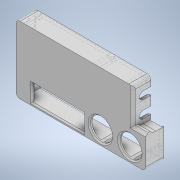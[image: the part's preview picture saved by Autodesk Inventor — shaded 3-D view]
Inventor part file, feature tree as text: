
AUTODESK INVENTOR PART (.ipt)
format: ipt  version: 2021 (Build 250183000, 183)  size: 477,696 bytes
history: native  units: mm
features: sketch x21, extrude x19, fillet x4, chamfer x4, hole x2
ambient origin geometry x8: Origin, YZ Plane, XZ Plane, XY Plane, X Axis, Y Axis, Z Axis, Center Point
bodies: Solid1 (feature_tree)
feature tree (50):
  extrude  "Extrusion1"  Depth=52.0mm
  extrude  "Extrusion2"  Depth=50.0mm
  extrude  "Extrusion3"  Depth=2.0mm
  extrude  "Extrusion4"  Depth=2.0mm
  fillet  "Fillet1"  Radius=2.0mm
  chamfer  "Chamfer1"  Distance=12.0mm
  extrude  "Extrusion5"  Depth=10.4mm
  extrude  "Extrusion6"  Depth=10.4mm
  extrude  "Extrusion7"  Depth=17.0mm
  extrude  "Extrusion8"  Depth=2.0mm
  extrude  "Extrusion9"  Depth=2.0mm
  chamfer  "Chamfer2"  Distance=2.0mm
  fillet  "Fillet2"  Radius=3.0mm
  extrude  "Extrusion10"  Depth=2.0mm
  fillet  "Fillet3"  Radius=29.0mm
  chamfer  "Chamfer3"  Distance=20.0mm
  extrude  "Extrusion11"  Depth=2.0mm TaperAngle=0.0deg
  extrude  "Extrusion12"  Depth=11.0mm
  hole  "Hole1"  [1 undecoded]
  extrude  "Extrusion13"  TaperAngle=0.0deg  [1 undecoded]
  hole  "Hole2"  [1 undecoded]
  extrude  "Extrusion14"  Depth=12.0mm
  extrude  "Extrusion15"  Depth=2.0mm TaperAngle=45.0deg
  extrude  "Extrusion16"  Depth=3.0mm
  extrude  "Extrusion17"  Depth=2.0mm
  extrude  "Extrusion20"  Depth=2.0mm
  fillet  "Fillet4"  Radius=14.0mm
  extrude  "Extrusion21"  Depth=2.0mm
  chamfer  "Chamfer6"  Distance=2.0mm
  sketch  "Sketch1"  dims[d0=100.0mm d1=52.0mm]
  sketch  "Sketch2"  dims[d2=26.0mm d3=50.0mm]
  sketch  "Sketch3"  dims[d4=2.0mm d5=0.0mm d6=2.0mm]
  sketch  "Sketch4"  dims[d7=2.0mm d8=2.0mm d9=2.0mm d10=12.0mm d11=0.0mm]
  sketch  "Sketch5"  dims[d12=65.0mm d13=10.4mm]
  sketch  "Sketch6"  dims[d14=87.75mm d15=10.4mm]
  sketch  "Sketch7"  dims[d16=17.0mm d17=17.0mm]
  sketch  "Sketch8"  dims[d18=2.0mm d19=0.0mm d20=40.0mm]
  sketch  "Sketch9"  dims[d21=13.0mm d22=2.0mm]
  sketch  "Sketch10"  dims[d23=12.0mm d24=2.0mm d25=0.0mm d26=3.0mm]
  sketch  "Sketch11"  dims[d27=1.0mm d28=2.0mm d29=45.0deg d30=88.0mm d31=29.0mm]
  sketch  "Sketch12"  dims[d32=23.0mm d33=20.0mm d34=0.0mm]
  sketch  "Sketch13"  dims[d35=2.0mm d36=0.0mm d37=2.0mm d38=0.0mm]
  sketch  "Sketch14"  dims[d39=11.0mm d40=11.0mm]
  sketch  "Sketch15"  dims[d41=42.0mm d42=29.0mm]
  sketch  "Sketch16"  dims[d43=6.0mm d44=0.0mm]
  sketch  "Sketch17"  dims[d45=5.8mm d46=5.8mm]
  sketch  "Sketch18"  dims[d47=2.0mm d48=0.0mm d49=12.0mm]
  sketch  "Sketch19"  dims[d50=20.0mm d51=0.0mm d52=2.0mm d53=2.0mm d54=45.0deg]
  sketch  "Sketch22"  dims[d55=3.0mm d56=30.0mm]
  sketch  "Sketch23"  dims[d57=40.0mm d58=3.5mm d59=6.0mm d60=14.0mm d61=16.0mm d62=2.0mm d63=0.0mm d64=1.0mm d65=1.0mm d66=2.0mm d67=45.0deg d68=3.0mm d69=49.0mm d70=60.0mm d71=49.0mm d72=85.0mm d73=49.0mm d74=2.0mm d75=2.0mm d76=2.0mm d77=5.0mm d78=5.0mm d79=5.0mm d80=12.0mm d81=0.0mm d82=3.0mm d83=3.0mm d84=2.0mm d85=5.0mm d86=12.0mm d87=0.0mm d88=2.0mm d89=6.0mm d90=4.0mm d91=2.0mm d92=90.0deg d93=6.5mm d94=20.594885mm d95=8.0mm d96=97.0mm d97=4.2mm d98=12.0mm d99=0.0mm d100=2.0mm d101=6.0mm d102=4.0mm d103=2.0mm d104=90.0deg d105=6.5mm d106=20.594885mm d107=6.0mm d108=5.8mm d109=5.8mm d110=2.0mm d111=11.0mm d112=0.0mm d113=1.0mm d114=0.0mm d115=2.0mm d116=10.0mm d117=0.0mm d118=0.0mm d119=1.0mm d120=0.0mm d150=17.0mm d151=17.0mm d152=12.0mm d153=0.0mm d160=2.0mm d161=5.0mm d162=1.0mm d163=1.0mm d164=11.0mm d165=0.0mm d166=4.0mm d167=2.0mm d168=45.0deg]
note: 3 required parameter values undecoded (feature->parameter linkage not recoverable at this tier; creation-order binding heuristic only, values carry confidence <= 0.55)
